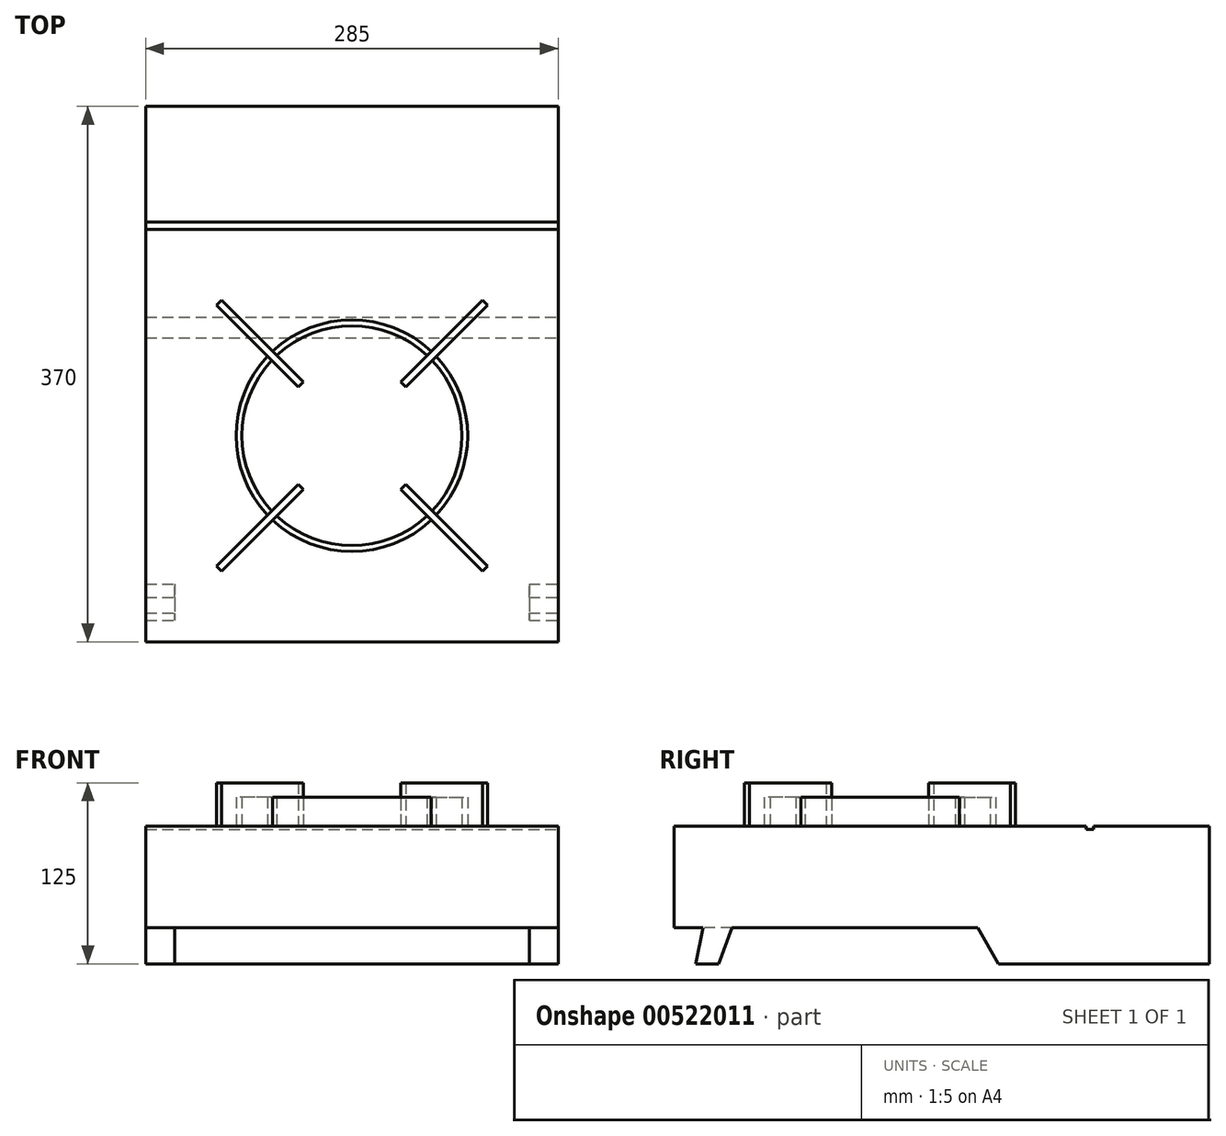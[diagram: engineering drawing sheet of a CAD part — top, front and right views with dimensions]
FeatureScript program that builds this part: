
annotation { "Feature Type Name" : "Feature", "Feature Type Description" : "" }
export const myFeature = defineFeature(function(context is Context, id is Id, definition is map)
    precondition{}
    {
        {
            var Q0;
            Q0=qCreatedBy(makeId("Top.planeOp"),FACE);
            var sketch = newSketch(context, id + "F0", { "sketchPlane" : qUnion([Q0])});
            skLineSegment(sketch, "E0.bottom", {"start": v(0, 0) * mm, "end": v(-285, 0) * mm});
            skLineSegment(sketch, "E0.top", {"start": v(0, 370) * mm, "end": v(-285, 370) * mm});
            skLineSegment(sketch, "E0.left", {"start": v(0, 0) * mm, "end": v(0, 370) * mm});
            skLineSegment(sketch, "E0.right", {"start": v(-285, 0) * mm, "end": v(-285, 370) * mm});
            skSolve(sketch);
        }
        {
            var Q0;
            Q0=makeQuery(id+"F0.imprint","IMPRINT",FACE,{"disambiguationData":[TD([[makeQuery(id+"F0.imprint","IMPRINT",EDGE,{"derivedFrom":sQuery(id+"F0.wireOp",EDGE,"E0.bottom")}),-1.0]])]});
            extrude(context, id + "F1", {"entities" : qUnion([Q0]), "depth" : (125 - 30) * mm, "offsetDistance" : 25 * mm});
        }
        {
            var Q0;
            Q0=makeQuery(id+"F1.opExtrude","CAP_FACE",FACE,{"disambiguationData":[OSD([sQuery(id+"F0.wireOp",EDGE,"E0.bottom"),sQuery(id+"F0.wireOp",EDGE,"E0.top"),sQuery(id+"F0.wireOp",EDGE,"E0.left"),sQuery(id+"F0.wireOp",EDGE,"E0.right")])],"isStart":false});
            var sketch = newSketch(context, id + "F2", { "sketchPlane" : qUnion([Q0])});
            skLineSegment(sketch, "E1.bottom", {"start": v(-285, 285) * mm, "end": v(0, 285) * mm});
            skLineSegment(sketch, "E1.top", {"start": v(-285, 290) * mm, "end": v(0, 290) * mm});
            skLineSegment(sketch, "E1.left", {"start": v(-285, 285) * mm, "end": v(-285, 290) * mm});
            skLineSegment(sketch, "E1.right", {"start": v(0, 285) * mm, "end": v(0, 290) * mm});
            skSolve(sketch);
        }
        {
            var Q0;
            Q0=makeQuery(id+"F2.imprint","IMPRINT",FACE,{"disambiguationData":[TD([[makeQuery(id+"F2.imprint","IMPRINT",EDGE,{"derivedFrom":sQuery(id+"F2.wireOp",EDGE,"E1.bottom")}),1.0]])]});
            extrude(context, id + "F3", {"entities" : qUnion([Q0]), "operationType" : NewBodyOperationType.REMOVE, "oppositeDirection" : true, "depth" : 2 * mm, "offsetDistance" : 25 * mm});
        }
        {
            var Q0;
            {var subQ0=sQuery(id+"F0.wireOp",EDGE,"E0.bottom");var subQ1=sQuery(id+"F0.wireOp",EDGE,"E0.right");var subQ2=sQuery(id+"F0.wireOp",EDGE,"E0.left");Q0=makeQuery(id+"F3.boolean.opBoolean","SPLIT",FACE,{"disambiguationData":[TD([makeQuery(id+"F1.opExtrude","SWEPT_FACE",FACE,{"disambiguationData":[OSD([subQ0])]})])],"derivedFrom":makeQuery(id+"F1.opExtrude","CAP_FACE",FACE,{"disambiguationData":[OSD([subQ0,sQuery(id+"F0.wireOp",EDGE,"E0.top"),subQ2,subQ1])],"isStart":false})});}
            var sketch = newSketch(context, id + "F4", { "sketchPlane" : qUnion([Q0])});
            skLineSegment(sketch, "E2", {"start": v(-142.5, 0) * mm, "end": v(-142.5, 285) * mm, "construction": true});
            skLineSegment(sketch, "E3", {"start": v(-285, 142.5) * mm, "end": v(0, 142.5) * mm, "construction": true});
            skCircle(sketch, "E4", {"center": v(-142.5, 142.5) * mm, "radius": 80 * mm});
            skCircle(sketch, "E5", {"center": v(-142.5, 142.5) * mm, "radius": 76 * mm});
            skLineSegment(sketch, "E6", {"start": v(-176.09, 105.38) * mm, "end": v(-179.62, 108.91) * mm});
            skLineSegment(sketch, "E7", {"start": v(-179.62, 108.91) * mm, "end": v(-236.17, 52.36) * mm});
            skLineSegment(sketch, "E8", {"start": v(-236.17, 52.36) * mm, "end": v(-232.64, 48.83) * mm});
            skLineSegment(sketch, "E9", {"start": v(-232.64, 48.83) * mm, "end": v(-176.09, 105.38) * mm});
            skLineSegment(sketch, "E10", {"start": v(-177.86, 107.14) * mm, "end": v(-142.5, 142.5) * mm, "construction": true});
            skLineSegment(sketch, "E11.1.0", {"start": v(-48.83, 52.36) * mm, "end": v(-105.38, 108.91) * mm});
            skLineSegment(sketch, "E11.1.1", {"start": v(-108.91, 105.38) * mm, "end": v(-52.36, 48.83) * mm});
            skLineSegment(sketch, "E11.1.2", {"start": v(-52.36, 48.83) * mm, "end": v(-48.83, 52.36) * mm});
            skLineSegment(sketch, "E11.1.3", {"start": v(-105.38, 108.91) * mm, "end": v(-108.91, 105.38) * mm});
            skLineSegment(sketch, "E11.2.0", {"start": v(-52.36, 236.17) * mm, "end": v(-108.91, 179.62) * mm});
            skLineSegment(sketch, "E11.2.1", {"start": v(-105.38, 176.09) * mm, "end": v(-48.83, 232.64) * mm});
            skLineSegment(sketch, "E11.2.2", {"start": v(-48.83, 232.64) * mm, "end": v(-52.36, 236.17) * mm});
            skLineSegment(sketch, "E11.2.3", {"start": v(-108.91, 179.62) * mm, "end": v(-105.38, 176.09) * mm});
            skLineSegment(sketch, "E11.3.0", {"start": v(-236.17, 232.64) * mm, "end": v(-179.62, 176.09) * mm});
            skLineSegment(sketch, "E11.3.1", {"start": v(-176.09, 179.62) * mm, "end": v(-232.64, 236.17) * mm});
            skLineSegment(sketch, "E11.3.2", {"start": v(-232.64, 236.17) * mm, "end": v(-236.17, 232.64) * mm});
            skLineSegment(sketch, "E11.3.3", {"start": v(-179.62, 176.09) * mm, "end": v(-176.09, 179.62) * mm});
            skSolve(sketch);
        }
        {
            var Q0;
            {var subQ5=sQuery(id+"F4.wireOp",EDGE,"E8");Q0=makeQuery(id+"F4.imprint","IMPRINT",FACE,{"disambiguationData":[TD([[makeQuery(id+"F4.imprint","IMPRINT",EDGE,{"derivedFrom":subQ5}),1.0]])]});}
            var Q1;
            {var subQ0=sQuery(id+"F4.wireOp",EDGE,"E7");var subQ1=sQuery(id+"F4.wireOp",EDGE,"E4");var subQ2=makeQuery(id+"F4.imprint","INTERSECT",VERTEX,{"derivedFrom":[subQ1,subQ0]});Q1=makeQuery(id+"F4.imprint","IMPRINT",FACE,{"disambiguationData":[TD([[makeQuery(id+"F4.imprint","IMPRINT",EDGE,{"disambiguationData":[TD([[subQ2,-1.0]])],"derivedFrom":subQ1}),1.0]])]});}
            var Q2;
            {var subQ5=sQuery(id+"F4.wireOp",EDGE,"E6");Q2=makeQuery(id+"F4.imprint","IMPRINT",FACE,{"disambiguationData":[TD([[makeQuery(id+"F4.imprint","IMPRINT",EDGE,{"derivedFrom":subQ5}),1.0]])]});}
            var Q3;
            {var subQ5=sQuery(id+"F4.wireOp",EDGE,"E11.1.3");Q3=makeQuery(id+"F4.imprint","IMPRINT",FACE,{"disambiguationData":[TD([[makeQuery(id+"F4.imprint","IMPRINT",EDGE,{"derivedFrom":subQ5}),1.0]])]});}
            var Q4;
            {var subQ0=sQuery(id+"F4.wireOp",EDGE,"E11.1.1");var subQ1=sQuery(id+"F4.wireOp",EDGE,"E4");var subQ2=makeQuery(id+"F4.imprint","INTERSECT",VERTEX,{"derivedFrom":[subQ1,subQ0]});Q4=makeQuery(id+"F4.imprint","IMPRINT",FACE,{"disambiguationData":[TD([[makeQuery(id+"F4.imprint","IMPRINT",EDGE,{"disambiguationData":[TD([[subQ2,-1.0]])],"derivedFrom":subQ1}),1.0]])]});}
            var Q5;
            {var subQ5=sQuery(id+"F4.wireOp",EDGE,"E11.1.2");Q5=makeQuery(id+"F4.imprint","IMPRINT",FACE,{"disambiguationData":[TD([[makeQuery(id+"F4.imprint","IMPRINT",EDGE,{"derivedFrom":subQ5}),1.0]])]});}
            var Q6;
            {var subQ5=sQuery(id+"F4.wireOp",EDGE,"E11.3.2");Q6=makeQuery(id+"F4.imprint","IMPRINT",FACE,{"disambiguationData":[TD([[makeQuery(id+"F4.imprint","IMPRINT",EDGE,{"derivedFrom":subQ5}),1.0]])]});}
            var Q7;
            {var subQ0=sQuery(id+"F4.wireOp",EDGE,"E11.3.1");var subQ1=sQuery(id+"F4.wireOp",EDGE,"E4");var subQ2=makeQuery(id+"F4.imprint","INTERSECT",VERTEX,{"derivedFrom":[subQ1,subQ0]});Q7=makeQuery(id+"F4.imprint","IMPRINT",FACE,{"disambiguationData":[TD([[makeQuery(id+"F4.imprint","IMPRINT",EDGE,{"disambiguationData":[TD([[subQ2,-1.0]])],"derivedFrom":subQ1}),1.0]])]});}
            var Q8;
            {var subQ5=sQuery(id+"F4.wireOp",EDGE,"E11.3.3");Q8=makeQuery(id+"F4.imprint","IMPRINT",FACE,{"disambiguationData":[TD([[makeQuery(id+"F4.imprint","IMPRINT",EDGE,{"derivedFrom":subQ5}),1.0]])]});}
            var Q9;
            {var subQ5=sQuery(id+"F4.wireOp",EDGE,"E11.2.2");Q9=makeQuery(id+"F4.imprint","IMPRINT",FACE,{"disambiguationData":[TD([[makeQuery(id+"F4.imprint","IMPRINT",EDGE,{"derivedFrom":subQ5}),1.0]])]});}
            var Q10;
            {var subQ0=sQuery(id+"F4.wireOp",EDGE,"E11.2.0");var subQ1=sQuery(id+"F4.wireOp",EDGE,"E4");var subQ2=makeQuery(id+"F4.imprint","INTERSECT",VERTEX,{"derivedFrom":[subQ1,subQ0]});Q10=makeQuery(id+"F4.imprint","IMPRINT",FACE,{"disambiguationData":[TD([[makeQuery(id+"F4.imprint","IMPRINT",EDGE,{"disambiguationData":[TD([[subQ2,1.0]])],"derivedFrom":subQ1}),1.0]])]});}
            var Q11;
            {var subQ5=sQuery(id+"F4.wireOp",EDGE,"E11.2.3");Q11=makeQuery(id+"F4.imprint","IMPRINT",FACE,{"disambiguationData":[TD([[makeQuery(id+"F4.imprint","IMPRINT",EDGE,{"derivedFrom":subQ5}),1.0]])]});}
            extrude(context, id + "F5", {"entities" : qUnion([Q0, Q1, Q2, Q3, Q4, Q5, Q6, Q7, Q8, Q9, Q10, Q11]), "operationType" : NewBodyOperationType.ADD, "depth" : 30 * mm, "offsetDistance" : 25 * mm});
        }
        {
            var Q0;
            {var subQ0=sQuery(id+"F4.wireOp",EDGE,"E9");var subQ1=sQuery(id+"F4.wireOp",EDGE,"E4");var subQ2=makeQuery(id+"F4.imprint","INTERSECT",VERTEX,{"derivedFrom":[subQ1,subQ0]});Q0=makeQuery(id+"F4.imprint","IMPRINT",FACE,{"disambiguationData":[TD([[makeQuery(id+"F4.imprint","IMPRINT",EDGE,{"disambiguationData":[TD([[subQ2,-1.0]])],"derivedFrom":subQ1}),1.0]])]});}
            var Q1;
            {var subQ0=sQuery(id+"F4.wireOp",EDGE,"E11.3.0");var subQ1=sQuery(id+"F4.wireOp",EDGE,"E4");var subQ2=makeQuery(id+"F4.imprint","INTERSECT",VERTEX,{"derivedFrom":[subQ1,subQ0]});Q1=makeQuery(id+"F4.imprint","IMPRINT",FACE,{"disambiguationData":[TD([[makeQuery(id+"F4.imprint","IMPRINT",EDGE,{"disambiguationData":[TD([[subQ2,-1.0]])],"derivedFrom":subQ1}),1.0]])]});}
            var Q2;
            {var subQ0=sQuery(id+"F4.wireOp",EDGE,"E11.2.0");var subQ1=sQuery(id+"F4.wireOp",EDGE,"E4");var subQ2=makeQuery(id+"F4.imprint","INTERSECT",VERTEX,{"derivedFrom":[subQ1,subQ0]});Q2=makeQuery(id+"F4.imprint","IMPRINT",FACE,{"disambiguationData":[TD([[makeQuery(id+"F4.imprint","IMPRINT",EDGE,{"disambiguationData":[TD([[subQ2,-1.0]])],"derivedFrom":subQ1}),1.0]])]});}
            var Q3;
            {var subQ0=sQuery(id+"F4.wireOp",EDGE,"E11.2.1");var subQ1=sQuery(id+"F4.wireOp",EDGE,"E4");var subQ2=makeQuery(id+"F4.imprint","INTERSECT",VERTEX,{"derivedFrom":[subQ1,subQ0]});Q3=makeQuery(id+"F4.imprint","IMPRINT",FACE,{"disambiguationData":[TD([[makeQuery(id+"F4.imprint","IMPRINT",EDGE,{"disambiguationData":[TD([[subQ2,1.0]])],"derivedFrom":subQ1}),1.0]])]});}
            extrude(context, id + "F6", {"entities" : qUnion([Q0, Q1, Q2, Q3]), "operationType" : NewBodyOperationType.ADD, "depth" : 20 * mm, "offsetDistance" : 25 * mm});
        }
        {
            var Q0;
            Q0=makeQuery(id+"F1.opExtrude","SWEPT_FACE",FACE,{"disambiguationData":[OSD([sQuery(id+"F0.wireOp",EDGE,"E0.left")])]});
            var sketch = newSketch(context, id + "F7", { "sketchPlane" : qUnion([Q0])});
            skLineSegment(sketch, "E12", {"start": v(30.9, 0) * mm, "end": v(40, 25) * mm});
            skLineSegment(sketch, "E13", {"start": v(40, 25) * mm, "end": v(210, 25) * mm});
            skLineSegment(sketch, "E14", {"start": v(210, 25) * mm, "end": v(224.43, 0) * mm});
            skLineSegment(sketch, "E15", {"start": v(224.43, 0) * mm, "end": v(30.9, 0) * mm});
            skLineSegment(sketch, "E16", {"start": v(15, 0) * mm, "end": v(20, 25) * mm});
            skLineSegment(sketch, "E17", {"start": v(20, 25) * mm, "end": v(0, 25) * mm});
            skLineSegment(sketch, "E18", {"start": v(0, 25) * mm, "end": v(0, 0) * mm});
            skLineSegment(sketch, "E19", {"start": v(0, 0) * mm, "end": v(15, 0) * mm});
            skSolve(sketch);
        }
        {
            var Q0;
            Q0=makeQuery(id+"F7.imprint","IMPRINT",FACE,{"disambiguationData":[TD([[makeQuery(id+"F7.imprint","IMPRINT",EDGE,{"derivedFrom":sQuery(id+"F7.wireOp",EDGE,"E16")}),1.0]])]});
            var Q1;
            Q1=makeQuery(id+"F7.imprint","IMPRINT",FACE,{"disambiguationData":[TD([[makeQuery(id+"F7.imprint","IMPRINT",EDGE,{"derivedFrom":sQuery(id+"F7.wireOp",EDGE,"E12")}),-1.0]])]});
            extrude(context, id + "F8", {"entities" : qUnion([Q0, Q1]), "operationType" : NewBodyOperationType.REMOVE, "oppositeDirection" : true, "depth" : 406 * mm, "offsetDistance" : 25 * mm});
        }
        {
            var Q0;
            Q0=makeQuery(id+"F1.opExtrude","SWEPT_FACE",FACE,{"disambiguationData":[OSD([sQuery(id+"F0.wireOp",EDGE,"E0.bottom")])]});
            var sketch = newSketch(context, id + "F9", { "sketchPlane" : qUnion([Q0])});
            skLineSegment(sketch, "E20.bottom", {"start": v(-265, 25) * mm, "end": v(-20, 25) * mm});
            skLineSegment(sketch, "E20.top", {"start": v(-265, 0) * mm, "end": v(-20, 0) * mm});
            skLineSegment(sketch, "E20.left", {"start": v(-265, 25) * mm, "end": v(-265, 0) * mm});
            skLineSegment(sketch, "E20.right", {"start": v(-20, 25) * mm, "end": v(-20, 0) * mm});
            skSolve(sketch);
        }
        {
            var Q0;
            Q0=makeQuery(id+"F9.imprint","IMPRINT",FACE,{"disambiguationData":[TD([[makeQuery(id+"F9.imprint","IMPRINT",EDGE,{"derivedFrom":sQuery(id+"F9.wireOp",EDGE,"E20.bottom")}),-1.0]])]});
            extrude(context, id + "F10", {"entities" : qUnion([Q0]), "operationType" : NewBodyOperationType.REMOVE, "oppositeDirection" : true, "depth" : 81 * mm, "offsetDistance" : 25 * mm});
        }
    });
